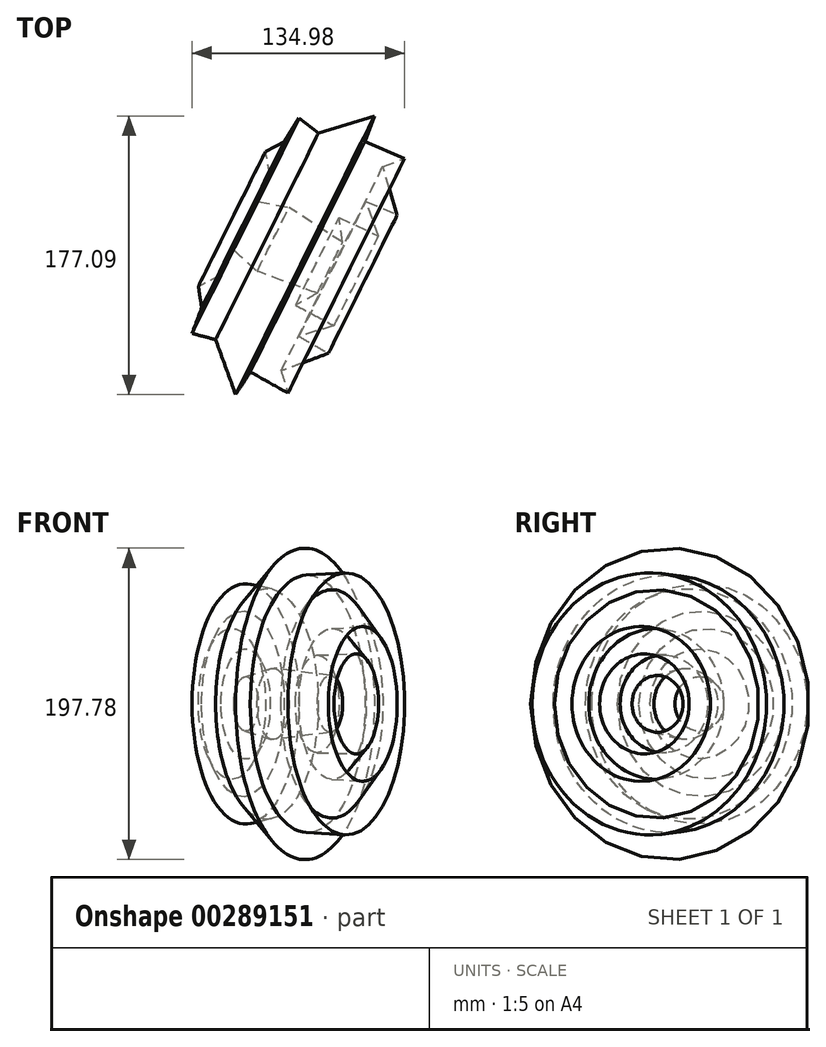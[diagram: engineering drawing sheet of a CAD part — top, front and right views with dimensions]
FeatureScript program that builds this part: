
annotation { "Feature Type Name" : "Feature", "Feature Type Description" : "" }
export const myFeature = defineFeature(function(context is Context, id is Id, definition is map)
    precondition{}
    {
        {
            var Q0;
            Q0=qCreatedBy(makeId("Top.planeOp"),FACE);
            var sketch = newSketch(context, id + "F0", { "sketchPlane" : qUnion([Q0])});
            skLineSegment(sketch, "E0", {"start": v(-72.13, 40.31) * mm, "end": v(-60.1, 46.78) * mm});
            skLineSegment(sketch, "E1", {"start": v(-60.1, 46.78) * mm, "end": v(-50.76, 61.5) * mm});
            skLineSegment(sketch, "E2", {"start": v(-50.76, 61.5) * mm, "end": v(-38.55, 51.99) * mm});
            skLineSegment(sketch, "E3", {"start": v(-38.55, 51.99) * mm, "end": v(-3, 62.94) * mm});
            skLineSegment(sketch, "E4", {"start": v(-3, 62.94) * mm, "end": v(-8.92, 46.78) * mm});
            skLineSegment(sketch, "E5", {"start": v(-8.92, 46.78) * mm, "end": v(16.23, 35.82) * mm});
            skLineSegment(sketch, "E6", {"start": v(16.23, 35.82) * mm, "end": v(2.4, 30.8) * mm});
            skLineSegment(sketch, "E7", {"start": v(2.4, 30.8) * mm, "end": v(11.56, 0.09) * mm});
            skLineSegment(sketch, "E8", {"start": v(11.56, 0.09) * mm, "end": v(-8.2, 8.53) * mm});
            skLineSegment(sketch, "E9", {"start": v(-8.2, 8.53) * mm, "end": v(-0.3, -13.38) * mm});
            skLineSegment(sketch, "E10", {"start": v(-0.3, -13.38) * mm, "end": v(-25.44, -1.7) * mm});
            skLineSegment(sketch, "E11", {"start": v(-25.44, -1.7) * mm, "end": v(-23.1, -17.33) * mm});
            skLineSegment(sketch, "E12", {"start": v(-23.1, -17.33) * mm, "end": v(-57.23, 4.76) * mm});
            skLineSegment(sketch, "E13", {"start": v(-57.23, 4.76) * mm, "end": v(-76.8, 8.53) * mm});
            skLineSegment(sketch, "E14", {"start": v(-76.8, 8.53) * mm, "end": v(-69.08, 24.51) * mm});
            skLineSegment(sketch, "E15", {"start": v(-69.08, 24.51) * mm, "end": v(-72.13, 40.31) * mm});
            skLineSegment(sketch, "E16", {"start": v(-94.22, 41.21) * mm, "end": v(-94.22, 7.99) * mm});
            skLineSegment(sketch, "E17", {"start": v(-80.77, -8.82) * mm, "end": v(-37.1, -30.54) * mm});
            skSolve(sketch);
        }
        {
            var Q0;
            Q0=makeQuery(id+"F0.imprint","IMPRINT",FACE,{"disambiguationData":[TD([[makeQuery(id+"F0.imprint","IMPRINT",EDGE,{"derivedFrom":sQuery(id+"F0.wireOp",EDGE,"E0")}),-1.0]])]});
            var Q1;
            Q1=sQuery(id+"F0.wireOp",EDGE,"E17");
            revolve(context, id + "F1", {"entities" : qUnion([Q0]), "axis" : qUnion([Q1]), "revolveType" : RevolveType.FULL});
        }
    });
